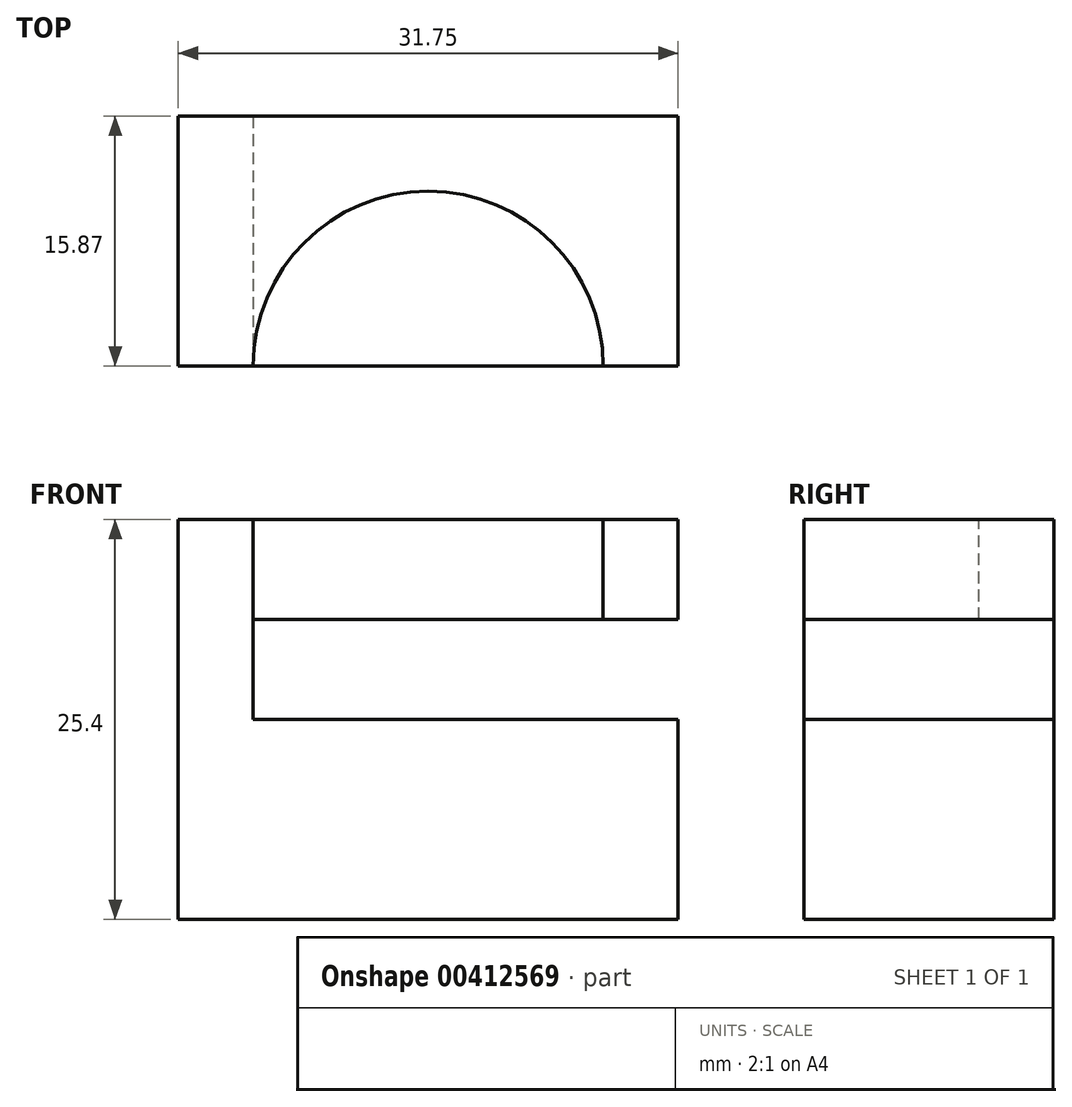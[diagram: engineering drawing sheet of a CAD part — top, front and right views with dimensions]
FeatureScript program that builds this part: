
annotation { "Feature Type Name" : "Feature", "Feature Type Description" : "" }
export const myFeature = defineFeature(function(context is Context, id is Id, definition is map)
    precondition{}
    {
        {
            var Q0;
            Q0=qCreatedBy(makeId("Top.planeOp"),FACE);
            var sketch = newSketch(context, id + "F0", { "sketchPlane" : qUnion([Q0])});
            skLineSegment(sketch, "E0.bottom", {"start": v(0, 0) * mm, "end": v(31.75, 0) * mm});
            skLineSegment(sketch, "E0.top", {"start": v(0, 31.75) * mm, "end": v(31.75, 31.75) * mm});
            skLineSegment(sketch, "E0.left", {"start": v(0, 0) * mm, "end": v(0, 31.75) * mm});
            skLineSegment(sketch, "E0.right", {"start": v(31.75, 0) * mm, "end": v(31.75, 31.75) * mm});
            skSolve(sketch);
        }
        {
            var Q0;
            Q0=makeQuery(id+"F0.imprint","IMPRINT",FACE,{"disambiguationData":[TD([[makeQuery(id+"F0.imprint","IMPRINT",EDGE,{"derivedFrom":sQuery(id+"F0.wireOp",EDGE,"E0.bottom")}),1.0]])]});
            extrude(context, id + "F1", {"entities" : qUnion([Q0]), "depth" : 25.4 * mm});
        }
        {
            var Q0;
            Q0=makeQuery(id+"F1.opExtrude","CAP_FACE",FACE,{"disambiguationData":[OSD([sQuery(id+"F0.wireOp",EDGE,"E0.bottom"),sQuery(id+"F0.wireOp",EDGE,"E0.top"),sQuery(id+"F0.wireOp",EDGE,"E0.left"),sQuery(id+"F0.wireOp",EDGE,"E0.right")])],"isStart":false});
            var sketch = newSketch(context, id + "F2", { "sketchPlane" : qUnion([Q0])});
            skArc(sketch, "E1", {"start": v(26.99, 9.53) * mm, "mid": v(15.87, 20.64) * mm, "end": v(4.76, 9.52) * mm});
            skPoint(sketch, "E1.centerSnap0", {"position": v(15.88, 31.75) * mm});
            skLineSegment(sketch, "E2", {"start": v(4.76, 9.52) * mm, "end": v(4.76, 0) * mm});
            skLineSegment(sketch, "E3", {"start": v(26.99, 9.53) * mm, "end": v(26.99, 0) * mm});
            skLineSegment(sketch, "E4", {"start": v(4.76, 0) * mm, "end": v(26.99, 0) * mm});
            skLineSegment(sketch, "E5", {"start": v(15.88, 9.52) * mm, "end": v(15.88, 31.75) * mm, "construction": true});
            skSolve(sketch);
        }
        {
            var Q0;
            Q0=makeQuery(id+"F2.imprint","IMPRINT",FACE,{"disambiguationData":[TD([[makeQuery(id+"F2.imprint","IMPRINT",EDGE,{"derivedFrom":sQuery(id+"F2.wireOp",EDGE,"E1")}),1.0]])]});
            extrude(context, id + "F3", {"entities" : qUnion([Q0]), "operationType" : NewBodyOperationType.REMOVE, "oppositeDirection" : true, "depth" : 12.7 * mm});
        }
        {
            var Q0;
            Q0=makeQuery(id+"F3.boolean.opBoolean","COPY",FACE,{"derivedFrom":makeQuery(id+"F3.opExtrude","CAP_FACE",FACE,{"disambiguationData":[OSD([sQuery(id+"F2.wireOp",EDGE,"E1"),sQuery(id+"F2.wireOp",EDGE,"E2"),sQuery(id+"F2.wireOp",EDGE,"E3"),sQuery(id+"F2.wireOp",EDGE,"E4")])],"isStart":false})});
            var sketch = newSketch(context, id + "F4", { "sketchPlane" : qUnion([Q0])});
            skLineSegment(sketch, "E6.bottom", {"start": v(4.76, 0) * mm, "end": v(31.75, 0) * mm});
            skLineSegment(sketch, "E6.top", {"start": v(4.76, 31.75) * mm, "end": v(31.75, 31.75) * mm});
            skLineSegment(sketch, "E6.left", {"start": v(4.76, 0) * mm, "end": v(4.76, 31.75) * mm});
            skLineSegment(sketch, "E6.right", {"start": v(31.75, 0) * mm, "end": v(31.75, 31.75) * mm});
            skSolve(sketch);
        }
        {
            var Q0;
            Q0 = qSketchRegion(id + "F4", true);
            extrude(context, id + "F5", {"entities" : qUnion([Q0]), "operationType" : NewBodyOperationType.REMOVE, "depth" : 6.35 * mm});
        }
        {
            var Q0;
            Q0=makeQuery(id+"F1.opExtrude","CAP_FACE",FACE,{"disambiguationData":[OSD([sQuery(id+"F0.wireOp",EDGE,"E0.bottom"),sQuery(id+"F0.wireOp",EDGE,"E0.top"),sQuery(id+"F0.wireOp",EDGE,"E0.left"),sQuery(id+"F0.wireOp",EDGE,"E0.right")])],"isStart":false});
            var sketch = newSketch(context, id + "F6", { "sketchPlane" : qUnion([Q0])});
            skLineSegment(sketch, "E7.bottom", {"start": v(0, 0) * mm, "end": v(31.75, 0) * mm});
            skLineSegment(sketch, "E7.top", {"start": v(0, 9.52) * mm, "end": v(31.75, 9.52) * mm});
            skLineSegment(sketch, "E7.left", {"start": v(0, 0) * mm, "end": v(0, 9.52) * mm});
            skLineSegment(sketch, "E7.right", {"start": v(31.75, 0) * mm, "end": v(31.75, 9.52) * mm});
            skSolve(sketch);
        }
        {
            var Q0;
            Q0 = qSketchRegion(id + "F6", true);
            extrude(context, id + "F7", {"entities" : qUnion([Q0]), "operationType" : NewBodyOperationType.REMOVE, "endBound" : BoundingType.THROUGH_ALL, "oppositeDirection" : true, "depth" : 25.4 * mm});
        }
        {
            var Q0;
            Q0=qCreatedBy(makeId("Top.planeOp"),FACE);
            var sketch = newSketch(context, id + "F8", { "sketchPlane" : qUnion([Q0])});
            skLineSegment(sketch, "E8.bottom", {"start": v(0, 31.75) * mm, "end": v(31.75, 31.75) * mm});
            skLineSegment(sketch, "E8.top", {"start": v(0, 25.4) * mm, "end": v(31.75, 25.4) * mm});
            skLineSegment(sketch, "E8.left", {"start": v(0, 31.75) * mm, "end": v(0, 25.4) * mm});
            skLineSegment(sketch, "E8.right", {"start": v(31.75, 31.75) * mm, "end": v(31.75, 25.4) * mm});
            skSolve(sketch);
        }
        {
            var Q0;
            Q0 = qSketchRegion(id + "F8", true);
            extrude(context, id + "F9", {"entities" : qUnion([Q0]), "operationType" : NewBodyOperationType.REMOVE, "endBound" : BoundingType.THROUGH_ALL, "depth" : 25.4 * mm});
        }
    });
